# Revit family: ewf_ewg-40_80eta2_fta2_jta2_lta2-pr(-50)_50Hz
name_source: partatom
category: 機械設備
units: mm (PartAtom-declared; Revit-internal decimal feet)

## family parameters
OmniClass タイトル = Industrial Ventilating Equipment
OmniClass 番号 = 23.75.35.21.17
パーツ タイプ = 標準
ロード時にボイドで切り取り = はい
丸型コネクタ寸法 = 直径を使用
作業面ベース = いいえ
共有 = いいえ
常に垂直 = はい
部屋計算ポイント = はい

## types (12) — shared parameters
IfcExportAs = IfcFanType
IfcExportType = TUBEAXIAL
MID風量 = 0.0 m³/h
MIN風量 = 0.0 m³/h
OmniClassCode = 23-33 31 19 11 17
URL = https://www.mitsubishielectric.co.jp
Uniclass2015Code = Pr_65_67_29_67
Uniclass2015Title = Propeller fans
Uniclass2015Version = Systems v1.9
ファンの種類 = 軸流羽根
仕様書バージョン = Version1.0
企業コード = 108420
分類コード = 50052503100110
周波数 = 50 Hz
呼称 = 有圧扇
極数 = 3
法定耐用年数 = 15
相 = 3
製品リリース年月 = 2022年6月1日
製品出荷対象 = 国内
製造元 = 三菱電機株式会社
設置方法 = 壁付
説明 = 産業用有圧換気扇 防錆タイプ
負荷分類 = 3_ファン類
運転質量 = 0.00 kg

## per-type parameters (varying)
| type | Depth | Height | MAX風量 | Width | オリフィス_Depth | オリフィス径 | フレームの厚さ | モデル | モーター径 | レグ_Depth | レグ_Height | レグ_Width | 価格 | 極 | 消費電力 | 羽根径 | 製品質量 | 質量 | 電動機出力 | 電圧 |
| EWF-40ETA2-PR_200V | 291  [stored 0.954724 ft] | 520  [stored 1.70604 ft] | 4800.0 m³/h | 520  [stored 1.70604 ft] | 99  [stored 0.324803 ft] | 480  [stored 1.5748 ft] | 10  [stored 0.0328084 ft] | EWF-40ETA2-PR | 131  [stored 0.42979 ft] | 262 | 413  [stored 1.35499 ft] | 413  [stored 1.35499 ft] | 193000 $ | 4 | 225 W | ∅400 | 14.30 kg | 17.16 kg | 400 W | 200 V |
| EWF-40ETA2-PR_220V | 291  [stored 0.954724 ft] | 520  [stored 1.70604 ft] | 4800.0 m³/h | 520  [stored 1.70604 ft] | 99  [stored 0.324803 ft] | 480  [stored 1.5748 ft] | 10  [stored 0.0328084 ft] | EWF-40ETA2-PR | 131  [stored 0.42979 ft] | 262 | 413  [stored 1.35499 ft] | 413  [stored 1.35499 ft] | 193000 $ | 4 | 245 W | ∅400 | 14.30 kg | 17.16 kg | 400 W | 220 V |
| EWF-50FTA2-PR_200V | 295 | 620 | 6900.0 m³/h | 620 | 84  [stored 0.275591 ft] | 590 | 10  [stored 0.0328084 ft] | EWF-50FTA2-PR | 131  [stored 0.42979 ft] | 266 | 522 | 522 | 241000 $ | 4 | 340 W | ∅500 | 19.60 kg | 23.52 kg | 750 W | 200 V |
| EWF-50FTA2-PR_220V | 295 | 620 | 6900.0 m³/h | 620 | 84  [stored 0.275591 ft] | 590 | 10  [stored 0.0328084 ft] | EWF-50FTA2-PR | 131  [stored 0.42979 ft] | 266 | 522 | 522 | 241000 $ | 4 | 365 W | ∅500 | 19.60 kg | 23.52 kg | 750 W | 220 V |
| EWG-50ETA2-PR_200V | 315 | 620 | 6060.0 m³/h | 620 | 84  [stored 0.275591 ft] | 590 | 10  [stored 0.0328084 ft] | EWG-50ETA2-PR | 131  [stored 0.42979 ft] | 286 | 514 | 514 | 224000 $ | 6 | 260 W | ∅500 | 18.30 kg | 21.96 kg | 400 W | 200 V |
| EWG-50ETA2-PR_220V | 315 | 620 | 6060.0 m³/h | 620 | 84  [stored 0.275591 ft] | 590 | 10  [stored 0.0328084 ft] | EWG-50ETA2-PR | 131  [stored 0.42979 ft] | 286 | 514 | 514 | 224000 $ | 6 | 290 W | ∅500 | 18.30 kg | 21.96 kg | 400 W | 220 V |
| EWG-60ETA2-PR_200V | 291  [stored 0.954724 ft] | 710 | 7860.0 m³/h | 710 | 119 | 703 | 10  [stored 0.0328084 ft] | EWG-60ETA2-PR | 131  [stored 0.42979 ft] | 262 | 604 | 604 | 249000 $ | 6 | 235 W | ∅600 | 20.00 kg | 24.00 kg | 400 W | 200 V |
| EWG-60ETA2-PR_220V | 291  [stored 0.954724 ft] | 710 | 7860.0 m³/h | 710 | 119 | 703 | 10  [stored 0.0328084 ft] | EWG-60ETA2-PR | 131  [stored 0.42979 ft] | 262 | 604 | 604 | 249000 $ | 6 | 250 W | ∅600 | 20.00 kg | 24.00 kg | 400 W | 220 V |
| EWG-60FTA2-PR_200V | 347 | 710 | 9420.0 m³/h | 710 | 119 | 703 | 10  [stored 0.0328084 ft] | EWG-60FTA2-PR | 163 | 309 | 612 | 612 | 296000 $ | 6 | 380 W | ∅600 | 25.90 kg | 31.08 kg | 750 W | 200 V |
| EWG-60FTA2-PR_220V | 347 | 710 | 9420.0 m³/h | 710 | 119 | 703 | 10  [stored 0.0328084 ft] | EWG-60FTA2-PR | 163 | 309 | 612 | 612 | 296000 $ | 6 | 406 W | ∅600 | 25.90 kg | 31.08 kg | 750 W | 220 V |
| EWG-70JTA2-PR-50 | 406 | 860 | 19500.0 m³/h | 860 | 90 | 846 | 35 | EWG-70JTA2-PR-50 | 289 | 325 | 714 | 714 | 688000 $ | 6 | 1220 W | ∅700 | 55.00 kg | 66.00 kg | 3700 W | 200 V |
| EWG-80LTA2-PR-50 | 450 | 950 | 27000.0 m³/h | 950 | 96 | 938 | 35 | EWG-80LTA2-PR-50 | 289 | 353 | 782 | 782 | 953000 $ | 6 | 2040 W | ∅800 | 73.00 kg | 87.60 kg | 7500 W | 200 V |

note: [stored X ft] marks values corroborated as IEEE doubles in the binary element streams (Revit-internal decimal feet)
